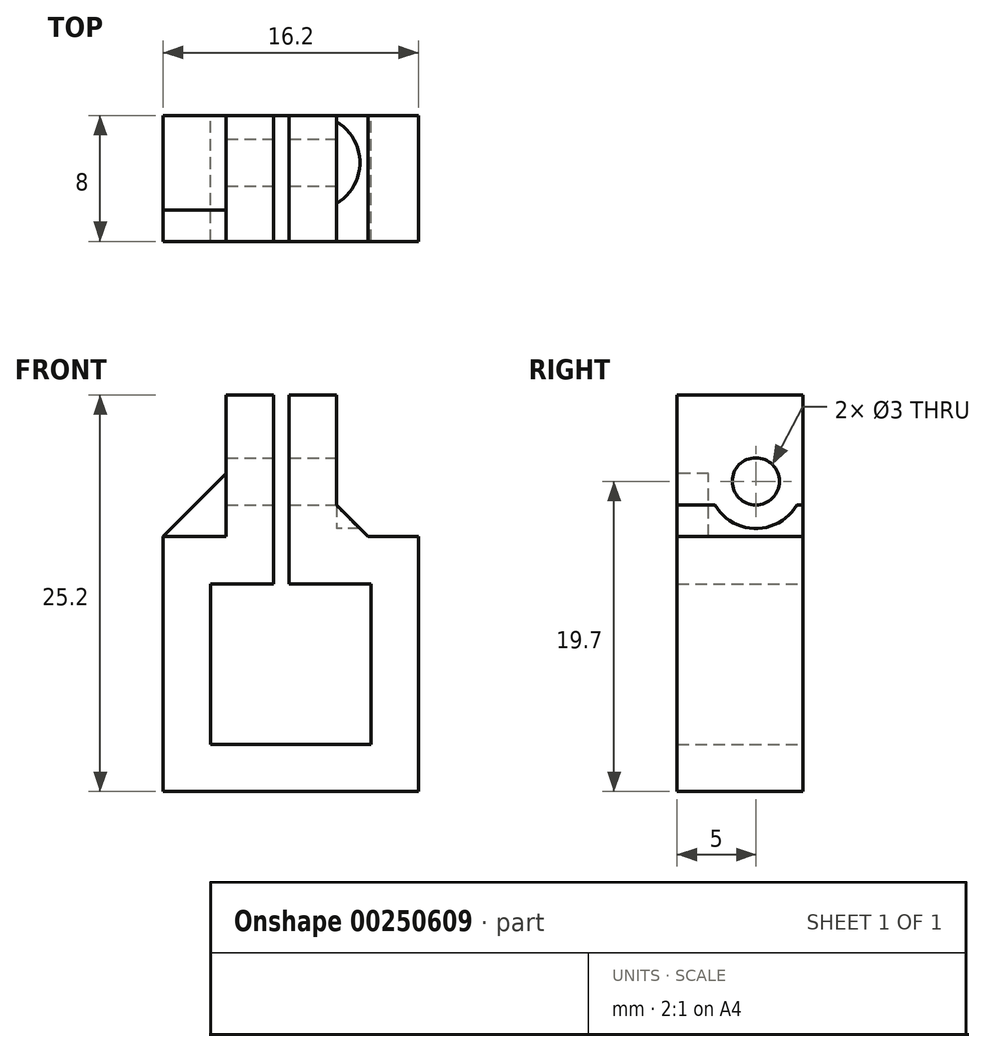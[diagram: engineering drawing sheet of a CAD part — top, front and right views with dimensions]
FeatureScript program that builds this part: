
annotation { "Feature Type Name" : "Feature", "Feature Type Description" : "" }
export const myFeature = defineFeature(function(context is Context, id is Id, definition is map)
    precondition{}
    {
        {
            var Q0;
            Q0=qCreatedBy(makeId("Front.planeOp"),FACE);
            var sketch = newSketch(context, id + "F0", { "sketchPlane" : qUnion([Q0])});
            skLineSegment(sketch, "E0.rect.bottom", {"start": v(5.1, -5.1) * mm, "end": v(-5.1, -5.1) * mm});
            skLineSegment(sketch, "E0.rect.top", {"start": v(5.1, 5.1) * mm, "end": v(-0.1, 5.1) * mm});
            skLineSegment(sketch, "E0.rect.left", {"start": v(5.1, -5.1) * mm, "end": v(5.1, 5.1) * mm});
            skLineSegment(sketch, "E0.rect.right", {"start": v(-5.1, -5.1) * mm, "end": v(-5.1, 5.1) * mm});
            skPoint(sketch, "E0.rect.middle", {"position": v(0, 0) * mm});
            skLineSegment(sketch, "E1.0", {"start": v(8.1, 8.1) * mm, "end": v(2.9, 8.1) * mm});
            skLineSegment(sketch, "E1.1", {"start": v(8.1, -8.1) * mm, "end": v(8.1, 8.1) * mm});
            skLineSegment(sketch, "E1.2", {"start": v(8.1, -8.1) * mm, "end": v(-8.1, -8.1) * mm});
            skLineSegment(sketch, "E1.3", {"start": v(-8.1, -8.1) * mm, "end": v(-8.1, 8.1) * mm});
            skLineSegment(sketch, "E2", {"start": v(-4.1, 8.1) * mm, "end": v(-4.1, 17.1) * mm});
            skLineSegment(sketch, "E3", {"start": v(-4.1, 17.1) * mm, "end": v(-1.1, 17.1) * mm});
            skLineSegment(sketch, "E4", {"start": v(-1.1, 17.1) * mm, "end": v(-1.1, 8.1) * mm});
            skLineSegment(sketch, "E5", {"start": v(-0.1, 17.1) * mm, "end": v(-0.1, 8.1) * mm});
            skLineSegment(sketch, "E6", {"start": v(-0.1, 17.1) * mm, "end": v(2.9, 17.1) * mm});
            skLineSegment(sketch, "E7", {"start": v(2.9, 17.1) * mm, "end": v(2.9, 8.1) * mm});
            skLineSegment(sketch, "E8", {"start": v(-4.1, 8.1) * mm, "end": v(-5.1, 8.1) * mm});
            skLineSegment(sketch, "E9", {"start": v(-8.1, 8.1) * mm, "end": v(-4.1, 8.1) * mm});
            skPoint(sketch, "E10.end.orphan", {"position": v(-5.1, 17.1) * mm});
            skLineSegment(sketch, "E11", {"start": v(-4.1, 5.1) * mm, "end": v(-5.1, 5.1) * mm});
            skLineSegment(sketch, "E12", {"start": v(-1.1, 8.1) * mm, "end": v(-1.1, 5.1) * mm});
            skLineSegment(sketch, "E13", {"start": v(-0.1, 8.1) * mm, "end": v(-0.1, 5.1) * mm});
            skPoint(sketch, "E13.endSnap0", {"position": v(0.5, 5.1) * mm});
            skLineSegment(sketch, "E14.trimOffspring", {"start": v(-1.1, 5.1) * mm, "end": v(-4.1, 5.1) * mm});
            skSolve(sketch);
        }
        {
            var Q0;
            Q0=qSketchRegion(id+"F0",true);
            extrude(context, id + "F1", {"entities" : qUnion([Q0]), "depth" : 8 * mm});
        }
        {
            var Q0;
            Q0=makeQuery(id+"F1.opExtrude","SWEPT_FACE",FACE,{"disambiguationData":[OSD([sQuery(id+"F0.wireOp",EDGE,"E4")])]});
            var sketch = newSketch(context, id + "F2", { "sketchPlane" : qUnion([Q0])});
            skCircle(sketch, "E15", {"center": v(-3, 11.6) * mm, "radius": 1.5 * mm});
            skPoint(sketch, "E15.centerSnap0", {"position": v(-7, 11.6) * mm});
            skPoint(sketch, "E15.centerSnap1", {"position": v(-3, 16.1) * mm});
            skSolve(sketch);
        }
        {
            var Q0;
            Q0=qSketchRegion(id+"F2",true);
            extrude(context, id + "F3", {"entities" : qUnion([Q0]), "operationType" : NewBodyOperationType.REMOVE, "endBound" : BoundingType.SYMMETRIC, "oppositeDirection" : true, "depth" : 25 * mm});
        }
        {
            var Q0;
            Q0=makeQuery(id+"F1.opExtrude","SWEPT_EDGE",EDGE,{"disambiguationData":[OSD([sQuery(id+"F0.wireOp",EDGE,"E1.0"),sQuery(id+"F0.wireOp",EDGE,"E7")])]});
            chamfer(context, id + "F4", {"entities" : qUnion([Q0]), "width" : 2 * mm, "tangentPropagation" : true});
        }
        {
            var Q0;
            Q0=makeQuery(id+"F1.opExtrude","SWEPT_FACE",FACE,{"disambiguationData":[OSD([sQuery(id+"F0.wireOp",EDGE,"E7")])]});
            var sketch = newSketch(context, id + "F5", { "sketchPlane" : qUnion([Q0])});
            skCircle(sketch, "E16", {"center": v(-3, 11.6) * mm, "radius": 3 * mm});
            skSolve(sketch);
        }
        {
            var Q0;
            Q0=qSketchRegion(id+"F5",true);
            extrude(context, id + "F6", {"entities" : qUnion([Q0]), "operationType" : NewBodyOperationType.REMOVE, "depth" : 4 * mm});
        }
        {
            var Q0;
            Q0=makeQuery(id+"F1.opExtrude","CAP_FACE",FACE,{"disambiguationData":[OSD([sQuery(id+"F0.wireOp",EDGE,"E0.rect.bottom"),sQuery(id+"F0.wireOp",EDGE,"E0.rect.top"),sQuery(id+"F0.wireOp",EDGE,"E0.rect.left"),sQuery(id+"F0.wireOp",EDGE,"E0.rect.right"),sQuery(id+"F0.wireOp",EDGE,"E1.0"),sQuery(id+"F0.wireOp",EDGE,"E1.1"),sQuery(id+"F0.wireOp",EDGE,"E1.2"),sQuery(id+"F0.wireOp",EDGE,"E1.3"),sQuery(id+"F0.wireOp",EDGE,"E2"),sQuery(id+"F0.wireOp",EDGE,"E3"),sQuery(id+"F0.wireOp",EDGE,"E4"),sQuery(id+"F0.wireOp",EDGE,"E5"),sQuery(id+"F0.wireOp",EDGE,"E6"),sQuery(id+"F0.wireOp",EDGE,"E7"),sQuery(id+"F0.wireOp",EDGE,"E9"),sQuery(id+"F0.wireOp",EDGE,"E11"),sQuery(id+"F0.wireOp",EDGE,"E12"),sQuery(id+"F0.wireOp",EDGE,"E13"),sQuery(id+"F0.wireOp",EDGE,"E14.trimOffspring")])],"isStart":false});
            var sketch = newSketch(context, id + "F7", { "sketchPlane" : qUnion([Q0])});
            skLineSegment(sketch, "E17", {"start": v(-8.1, 8.1) * mm, "end": v(-4.1, 12.1) * mm});
            skLineSegment(sketch, "E18", {"start": v(-8.1, 8.1) * mm, "end": v(-4.1, 8.1) * mm});
            skLineSegment(sketch, "E19", {"start": v(-4.1, 8.1) * mm, "end": v(-4.1, 12.1) * mm});
            skSolve(sketch);
        }
        {
            var Q0;
            Q0=qSketchRegion(id+"F7",true);
            extrude(context, id + "F8", {"entities" : qUnion([Q0]), "oppositeDirection" : true, "depth" : 2 * mm});
        }
    });
